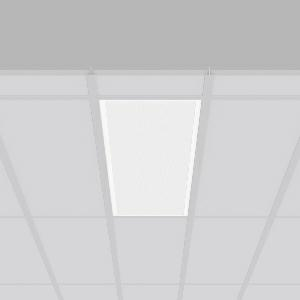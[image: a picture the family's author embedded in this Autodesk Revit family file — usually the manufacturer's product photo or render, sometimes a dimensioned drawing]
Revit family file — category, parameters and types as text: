
# Revit family: sidelite_eco_672368_002_04_deba
name_source: partatom
category: Lighting Fixtures
units: mm (PartAtom-declared; Revit-internal decimal feet)

## family parameters
Cut with Voids When Loaded = No
Host = Face
Light Source = No
Part Type = Normal
Room Calculation Point = No
Round Connector Dimension = Use Diameter
Shared = No

## types (1)
- SIDELITE ECO (1 x LED Modul 830, 3200 lm, 3000)
    Apparent Load = 29 VA
    CIE Flux Codes = 59 87 97 100 100
    Color Rendering = 80
    Color Temperature = 3000
    Default Elevation = 1800 mm
    Description = Series: SIDELITE ECO
Highly economical recessed luminaire with progressive LED technology. For escape route illumination. Frame made of aluminium, powder-coated. Diffuser plastic microprismatic. Lightguide and diffuser made of non-yellowing plastic (PMMA). Lateral light emission (RZB SIDELITE technology) for homogeneous light distribution. External driver. Self-contained system with automatic self-test and feedback to the RZB monitoring system MULTIDIGIT. External driver with simple plug-in locking system. Extended connection cable (1.90 m). 
Colour: white
Length: 1195 mm
Width: 295 mm
Cut-out length: 1170 mm
Cut-out width: 270 mm
Recess height: 160 mm
Luminaire: recess height: 40 mm
Weight: 4.4 kg
Operating mode: maintained power mode
Duration time: 3 h
Lamp: LED
Socket: without socket
Colour temperature: 3000K
Colour rendering index (CRI): 80
System power: 29 W
Rated luminous flux: 3200 lm
Luminous flux, emergency: 470 lm
System power, emergency: -
Control gear: Regulated power supply
Protection class: I
Type of protection: IP 40
    Height = 0 mm  [stored 0 ft]
    Lamp = 1 x LED Modul 830
    Lamp Light Flux = 3200 lm
    Lamp count = 1
    Length = 1195 mm
    Lifetime = 50000 h
    Luminous efficacy = 110 lm/W
    Manufacturer = RZB
    ModVariant = No
    Model = 672368.002.04
    Mounting Place = Ceiling
    Mounting Type = Recessed
    Number of Poles = 1
    OnlyDefault = Yes
    Power Factor = 1
    Product Name = SIDELITE ECO
    Product group = Recessed modular luminaires
    ProductGroupID = 406
    Protection Class = Protection class I
    Protection Degree = IP 40
    RLX_Detail_Level = 1
    RLX_Emergency_Light_Flux = 470 lm
    RLX_Emergency_Type = 3
    RLX_Emergency_Type_DB = Yes
    RlxData = <blob elided: 34745 chars, md5=625c0ae6>
    Socket = socket
    Standby Power = 0 W
    System Light Flux = 3200 lm
    System Power = 29 W
    Type Comments = Product without accessories
    Type Image = 312366.002.jpg
    URL = http://relux.com
    VarID = ---
    Voltage = 230 V
    Voltage Range = 220-240 V
    Weight = 0.00 kg
    Width = 295 mm

note: [stored X ft] marks values corroborated as IEEE doubles in the binary element streams (Revit-internal decimal feet)

## geometry (parser evidence)
native form markers: Blend x4, Sweep x12
no freeform markers — native parametric forms only
